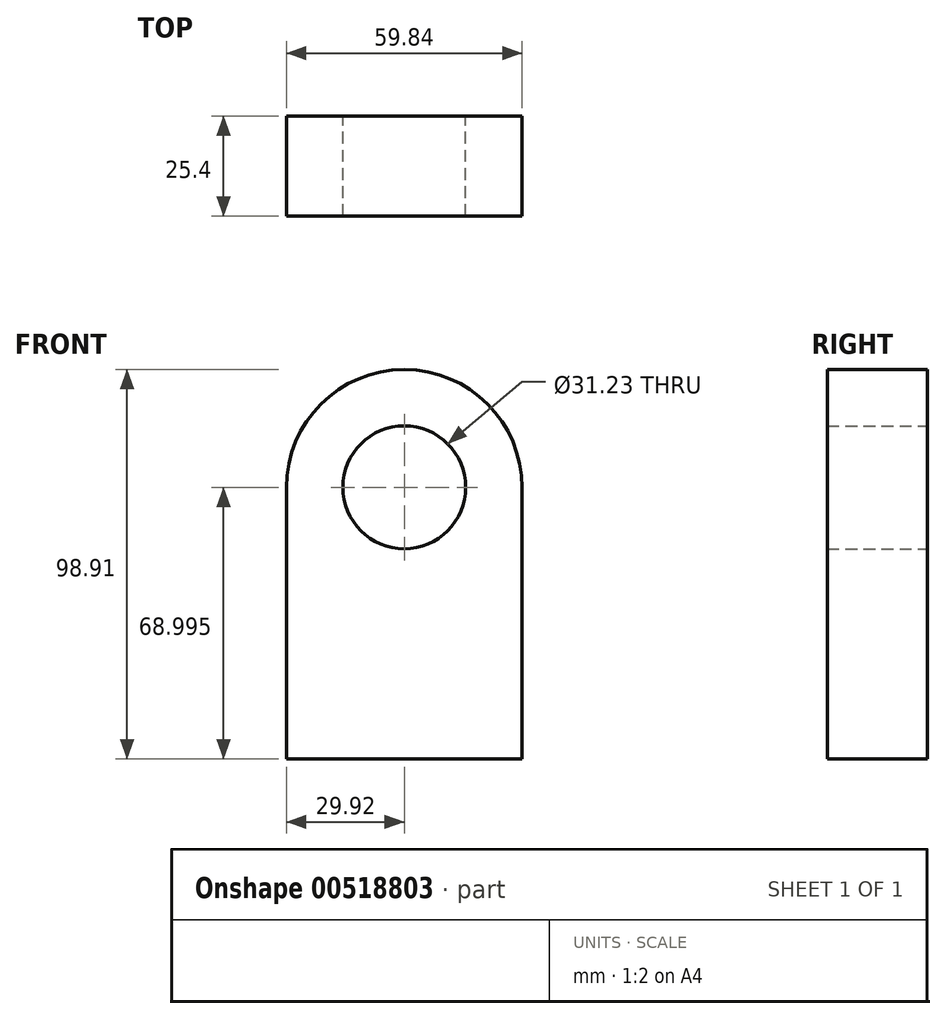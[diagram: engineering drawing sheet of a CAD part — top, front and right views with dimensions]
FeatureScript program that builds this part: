
annotation { "Feature Type Name" : "Feature", "Feature Type Description" : "" }
export const myFeature = defineFeature(function(context is Context, id is Id, definition is map)
    precondition{}
    {
        {
            var Q0;
            Q0=qCreatedBy(makeId("Front.planeOp"),FACE);
            var sketch = newSketch(context, id + "F0", { "sketchPlane" : qUnion([Q0])});
            skLineSegment(sketch, "E0.top", {"start": v(-29.92, -34.5) * mm, "end": v(29.92, -34.5) * mm});
            skLineSegment(sketch, "E0.left", {"start": v(-29.92, 34.5) * mm, "end": v(-29.92, -34.5) * mm});
            skLineSegment(sketch, "E0.right", {"start": v(29.92, 34.5) * mm, "end": v(29.92, -34.5) * mm});
            skPoint(sketch, "E0.middle", {"position": v(0, 0) * mm});
            skCircle(sketch, "E1", {"center": v(0, 34.5) * mm, "radius": 15.62 * mm});
            skArc(sketch, "E2", {"start": v(-29.92, 34.5) * mm, "mid": v(0, 64.41) * mm, "end": v(29.92, 34.5) * mm});
            skSolve(sketch);
        }
        {
            var Q0;
            Q0 = qSketchRegion(id + "F0", true);
            extrude(context, id + "F1", {"entities" : qUnion([Q0]), "depth" : 25.4 * mm});
        }
    });
